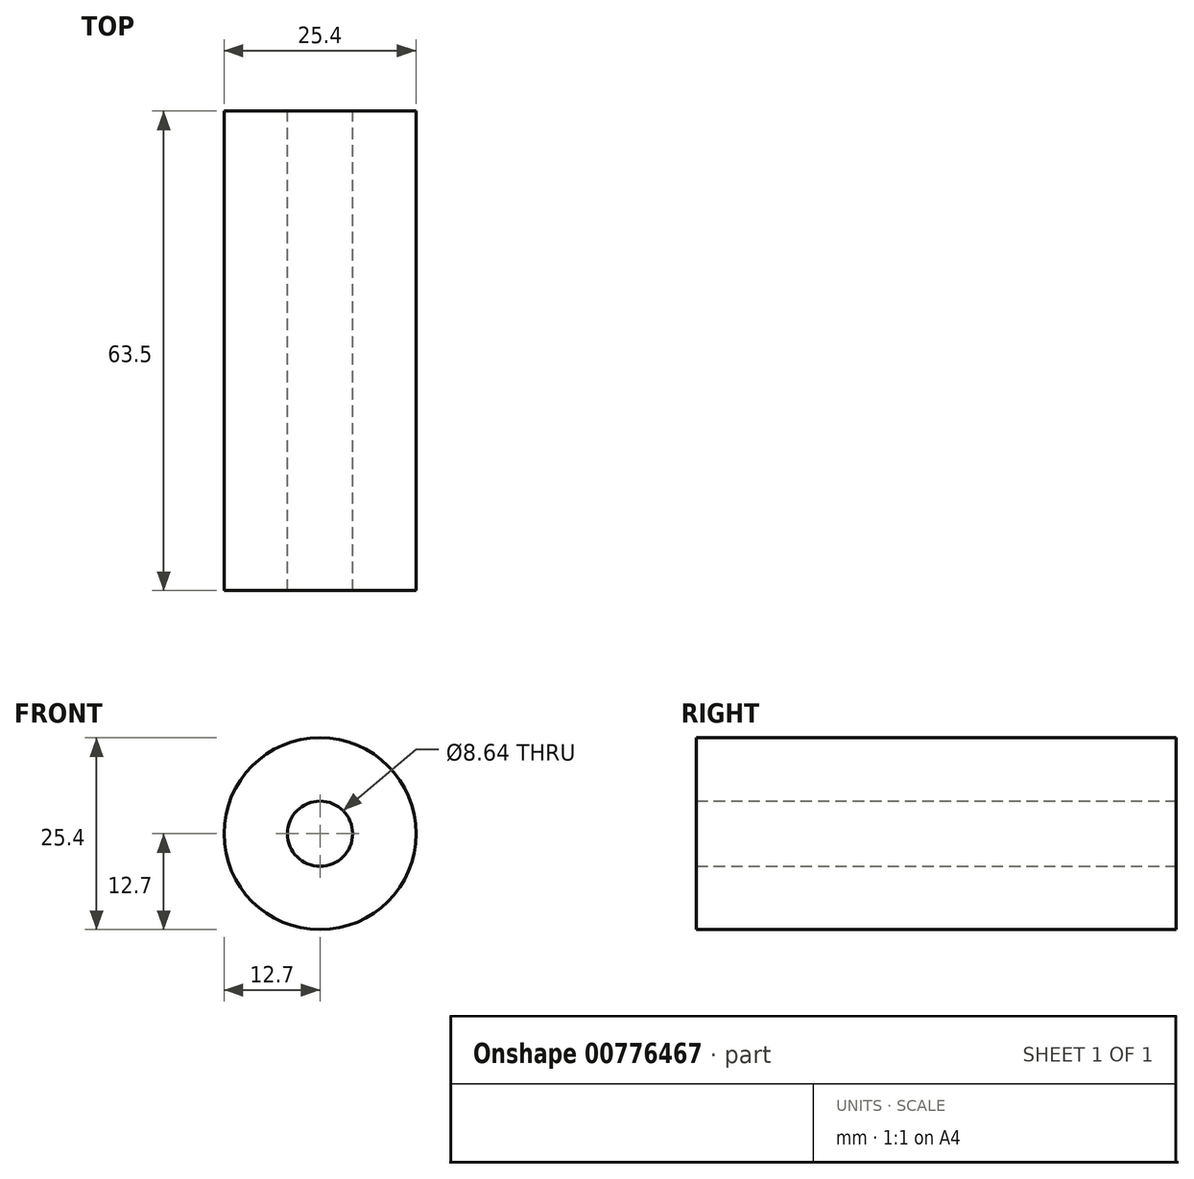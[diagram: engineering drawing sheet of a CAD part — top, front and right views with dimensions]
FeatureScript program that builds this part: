
annotation { "Feature Type Name" : "Feature", "Feature Type Description" : "" }
export const myFeature = defineFeature(function(context is Context, id is Id, definition is map)
    precondition{}
    {
        {
            var Q0;
            Q0=qCreatedBy(makeId("Front.planeOp"),FACE);
            var sketch = newSketch(context, id + "F0", { "sketchPlane" : qUnion([Q0])});
            skCircle(sketch, "E0", {"center": v(0, 0) * mm, "radius": 4.32 * mm});
            skCircle(sketch, "E1", {"center": v(0, 0) * mm, "radius": 12.7 * mm});
            skSolve(sketch);
        }
        {
            var Q0;
            Q0=qSketchRegion(id+"F0",true);
            extrude(context, id + "F1", {"entities" : qUnion([Q0]), "depth" : 63.5 * mm, "offsetDistance" : 25.4 * mm});
        }
    });
